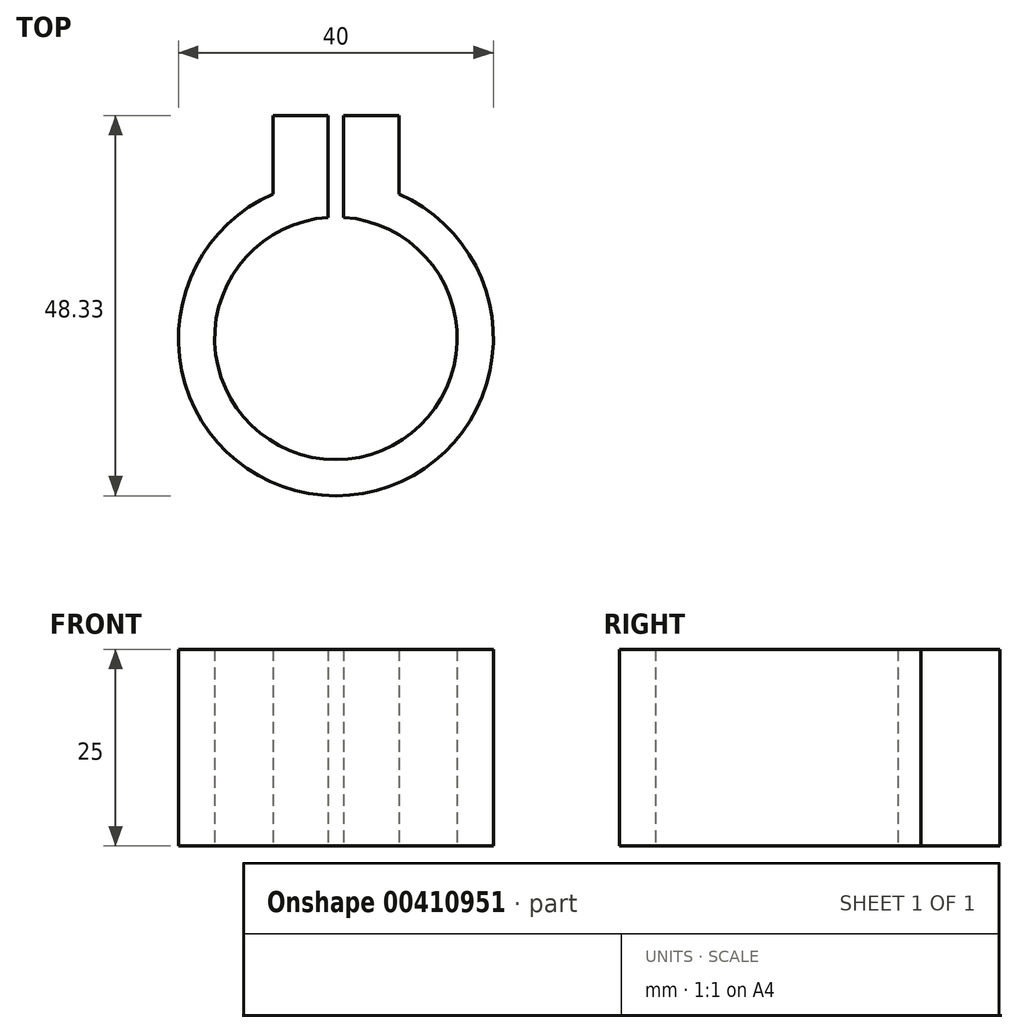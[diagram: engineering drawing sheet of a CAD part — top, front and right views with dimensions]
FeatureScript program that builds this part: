
annotation { "Feature Type Name" : "Feature", "Feature Type Description" : "" }
export const myFeature = defineFeature(function(context is Context, id is Id, definition is map)
    precondition{}
    {
        {
            var Q0;
            Q0=qCreatedBy(makeId("Top.planeOp"),FACE);
            var sketch = newSketch(context, id + "F0", { "sketchPlane" : qUnion([Q0])});
            skCircle(sketch, "E0", {"center": v(0, 0) * mm, "radius": 15.4 * mm});
            skPoint(sketch, "E0.centerSnap0", {"position": v(0, -20.02) * mm});
            skCircle(sketch, "E1", {"center": v(0, 0) * mm, "radius": 20 * mm});
            skLineSegment(sketch, "E2", {"start": v(-8, 18.33) * mm, "end": v(-8, 28.33) * mm});
            skLineSegment(sketch, "E3", {"start": v(8, 28.33) * mm, "end": v(8, 18.33) * mm});
            skPoint(sketch, "E4", {"position": v(0, 28.33) * mm});
            skLineSegment(sketch, "E5", {"start": v(-1, 28.33) * mm, "end": v(-1, 19.97) * mm});
            skLineSegment(sketch, "E6", {"start": v(1, 19.97) * mm, "end": v(1, 28.33) * mm});
            skLineSegment(sketch, "E7", {"start": v(-8, 28.33) * mm, "end": v(-1, 28.33) * mm});
            skLineSegment(sketch, "E8", {"start": v(-1, 28.33) * mm, "end": v(1, 28.33) * mm});
            skLineSegment(sketch, "E9", {"start": v(1, 28.33) * mm, "end": v(8, 28.33) * mm});
            skLineSegment(sketch, "E10", {"start": v(-1, 19.97) * mm, "end": v(-1, 15.37) * mm});
            skLineSegment(sketch, "E11", {"start": v(1, 19.97) * mm, "end": v(1, 15.37) * mm});
            skSolve(sketch);
        }
        {
            var Q0;
            {var subQ5=sQuery(id+"F0.wireOp",EDGE,"E10");Q0=makeQuery(id+"F0.imprint","IMPRINT",FACE,{"disambiguationData":[TD([[makeQuery(id+"F0.imprint","IMPRINT",EDGE,{"derivedFrom":subQ5}),-1.0]])]});}
            var Q1;
            {var subQ5=sQuery(id+"F0.wireOp",EDGE,"E11");Q1=makeQuery(id+"F0.imprint","IMPRINT",FACE,{"disambiguationData":[TD([[makeQuery(id+"F0.imprint","IMPRINT",EDGE,{"derivedFrom":subQ5}),1.0]])]});}
            var Q2;
            Q2=makeQuery(id+"F0.imprint","IMPRINT",FACE,{"disambiguationData":[TD([[makeQuery(id+"F0.imprint","IMPRINT",EDGE,{"derivedFrom":sQuery(id+"F0.wireOp",EDGE,"oEwtudDz-SjC8-hQNe-05ZD-RzdaNyCf03V4.top")}),1.0]])]});
            var Q3;
            Q3=makeQuery(id+"F0.imprint","IMPRINT",FACE,{"disambiguationData":[TD([[makeQuery(id+"F0.imprint","IMPRINT",EDGE,{"derivedFrom":sQuery(id+"F0.wireOp",EDGE,"oEwtudDz-SjC8-hQNe-05ZD-RzdaNyCf03V4.bottom")}),1.0]])]});
            var Q4;
            Q4=makeQuery(id+"F0.imprint","IMPRINT",FACE,{"disambiguationData":[TD([[makeQuery(id+"F0.imprint","IMPRINT",EDGE,{"derivedFrom":sQuery(id+"F0.wireOp",EDGE,"o0JP5JUT-JVZt-uN24-Py1k-0bSq06MwxqQO")}),-1.0]])]});
            var Q5;
            {var subQ0=sQuery(id+"F0.wireOp",EDGE,"E3");Q5=makeQuery(id+"F0.imprint","IMPRINT",FACE,{"disambiguationData":[TD([[makeQuery(id+"F0.imprint","IMPRINT",EDGE,{"derivedFrom":subQ0}),-1.0]])]});}
            var Q6;
            {var subQ0=sQuery(id+"F0.wireOp",EDGE,"E2");Q6=makeQuery(id+"F0.imprint","IMPRINT",FACE,{"disambiguationData":[TD([[makeQuery(id+"F0.imprint","IMPRINT",EDGE,{"derivedFrom":subQ0}),-1.0]])]});}
            extrude(context, id + "F1", {"entities" : qUnion([Q0, Q1, Q2, Q3, Q4, Q5, Q6]), "depth" : 25 * mm, "offsetDistance" : 25 * mm});
        }
    });
